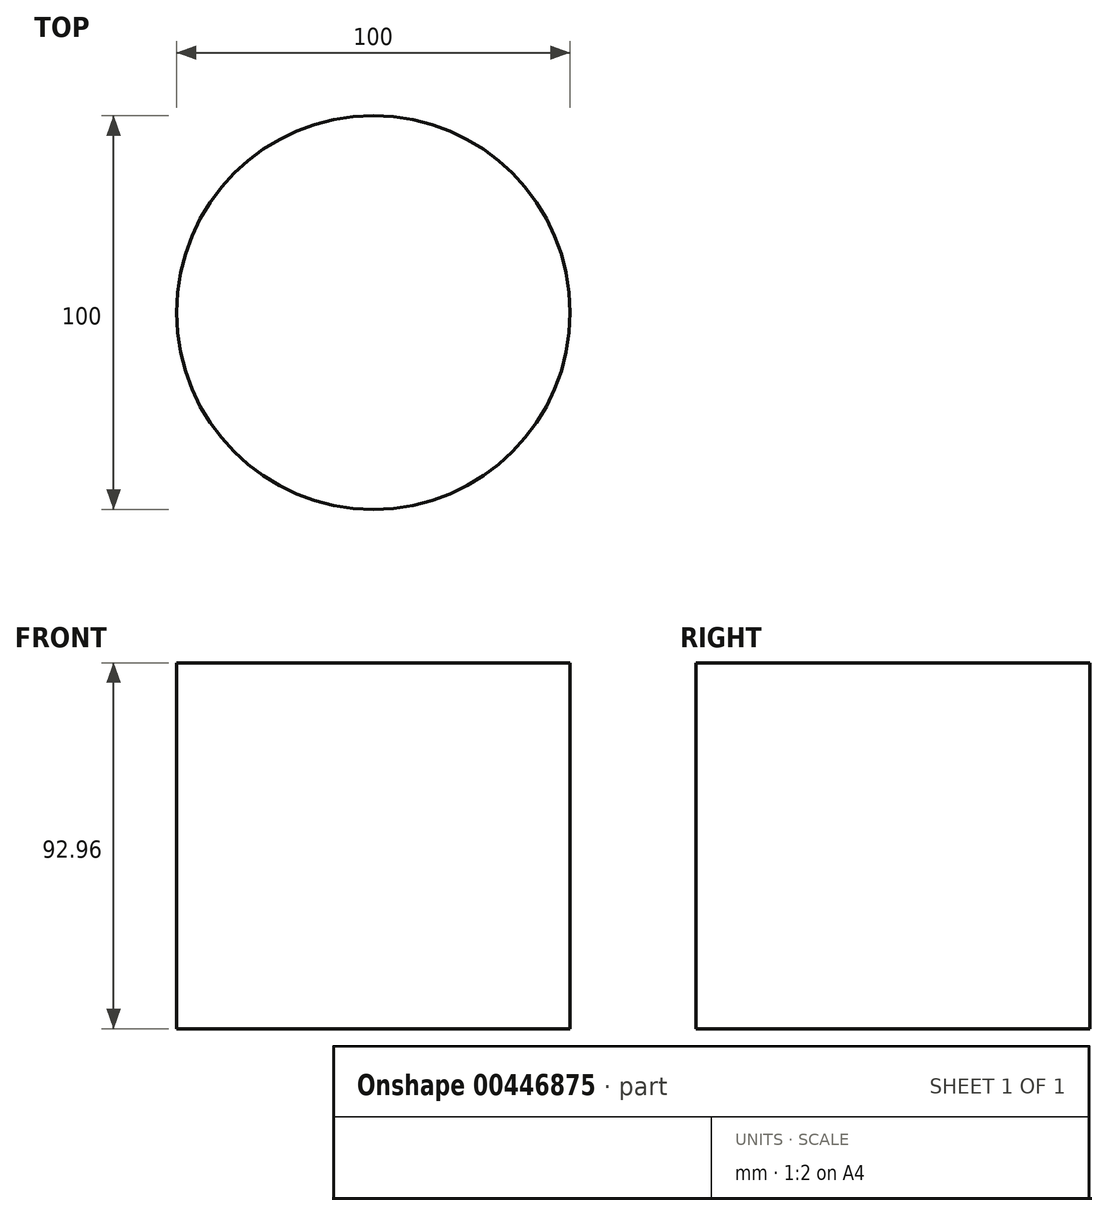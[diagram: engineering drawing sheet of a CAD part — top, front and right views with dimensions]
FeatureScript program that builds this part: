
annotation { "Feature Type Name" : "Feature", "Feature Type Description" : "" }
export const myFeature = defineFeature(function(context is Context, id is Id, definition is map)
    precondition{}
    {
        {
            var Q0;
            Q0=qCreatedBy(makeId("Top.planeOp"),FACE);
            var sketch = newSketch(context, id + "F0", { "sketchPlane" : qUnion([Q0])});
            skCircle(sketch, "E0", {"center": v(0, 0) * mm, "radius": 50 * mm});
            skSolve(sketch);
        }
        {
            var Q0;
            Q0=makeQuery(id+"F0.imprint","IMPRINT",FACE,{"disambiguationData":[TD([[makeQuery(id+"F0.imprint","IMPRINT",EDGE,{"derivedFrom":sQuery(id+"F0.wireOp",EDGE,"E0")}),1.0]])]});
            extrude(context, id + "F1", {"entities" : qUnion([Q0]), "depth" : 92.96 * mm});
        }
    });
